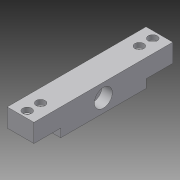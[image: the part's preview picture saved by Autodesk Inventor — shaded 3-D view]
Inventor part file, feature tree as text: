
AUTODESK INVENTOR PART (.ipt)
format: ipt  version: 2014 (Build 180170000, 170)  size: 144,384 bytes
history: native  units: in
note: dims shown in document units (in); Inventor stores cm internally (conversion verified against a paired STEP export)
features: sketch x4, projected_geometry x3, extrude x2, hole x2, plane x1, mirror x1
ambient origin geometry x8: Origin, YZ Plane, XZ Plane, XY Plane, X Axis, Y Axis, Z Axis, Center Point
bodies: Solid1 (feature_tree)
feature tree (13):
  extrude  "Extrusion1"  TaperAngle=0.0deg  [1 undecoded]
  plane  "Work Plane1"
  hole  "Hole1"  [1 undecoded]
  extrude  "Extrusion2"  Depth=0.65in
  mirror  "Mirror2"
  sketch  "Sketch7"  dims[d11=0.65in d12=0.7874in d14=0.1625in d15=0.7874in d17=0.1625in d20=0.136in d21=0.75in d22=0.219in d23=0.12in d24=0.5635in d25=1.0in d26=0.8108in d48=0.5in d71=0.266in d72=0.75in d73=0.438in d74=0.25in d75=0.5635in d76=1.0in d77=0.8108in]
  hole  "Hole6"  [1 undecoded]
  sketch  "Sketch2"  dims[d2=0.65in d3=0.0in]
  sketch  "Sketch4"  dims[d6=0.65in d7=0.65in]
  projected_geometry  "Projected Loop2"
  sketch  "Sketch5"  dims[d8=0.205in d9=0.0in d10=0.65in]
  projected_geometry  "Projected Loop3"
  projected_geometry  "Projected Loop4"
note: 3 required parameter values undecoded (feature->parameter linkage not recoverable at this tier; creation-order binding heuristic only, values carry confidence <= 0.55)
